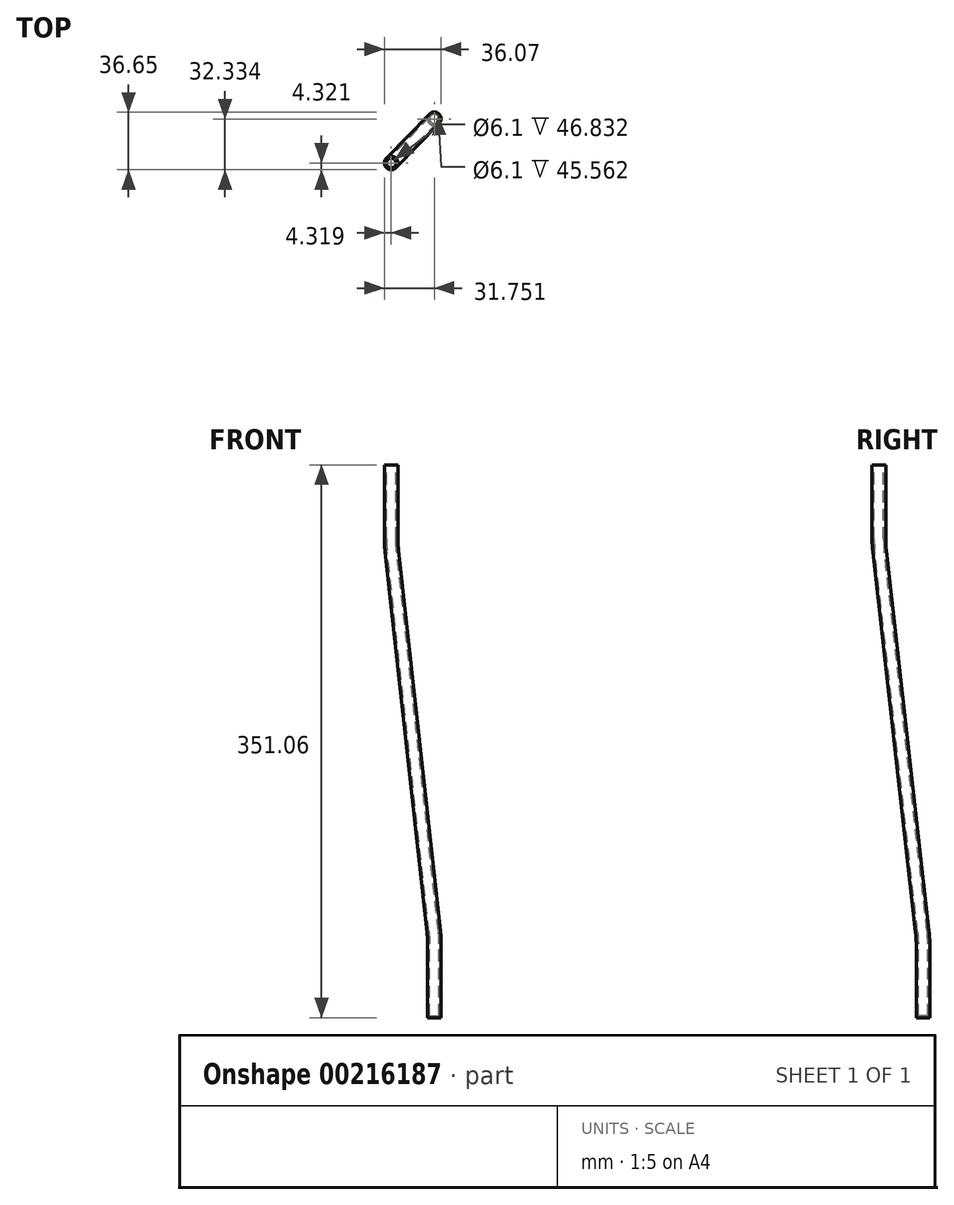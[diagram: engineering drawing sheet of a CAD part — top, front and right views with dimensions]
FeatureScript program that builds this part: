
annotation { "Feature Type Name" : "Feature", "Feature Type Description" : "" }
export const myFeature = defineFeature(function(context is Context, id is Id, definition is map)
    precondition{}
    {
        {
            var Q0;
            Q0=qCreatedBy(makeId("Top.planeOp"),FACE);
            var sketch = newSketch(context, id + "F0", { "sketchPlane" : qUnion([Q0])});
            skLineSegment(sketch, "E0", {"start": v(0, 0) * mm, "end": v(-395.7, 0) * mm});
            skLineSegment(sketch, "E1", {"start": v(-395.7, 0) * mm, "end": v(-395.7, 47.35) * mm});
            skLineSegment(sketch, "E2", {"start": v(0, 0) * mm, "end": v(-368.26, 0) * mm});
            skLineSegment(sketch, "E3", {"start": v(-368.26, 0) * mm, "end": v(-368.26, 75.36) * mm});
            skSolve(sketch);
        }
        {
            var Q0;
            Q0=sQuery(id+"F0.wireOp",EDGE,"E1");
            cPlane(context, id + "F1", {"entities" : qUnion([Q0]), "cplaneType" : CPlaneType.LINE_ANGLE, "offset" : 25.4 * mm, "angle" : 90 * degree, "width" : 152.4 * mm, "height" : 152.4 * mm});
        }
        {
            var Q0;
            Q0=qCreatedBy(id+"F1.planeOp",FACE);
            var sketch = newSketch(context, id + "F2", { "sketchPlane" : qUnion([Q0])});
            skLineSegment(sketch, "E4", {"start": v(47.35, 0) * mm, "end": v(47.35, 982.1) * mm});
            skLineSegment(sketch, "E5", {"start": v(47.35, 982.1) * mm, "end": v(21.95, 982.1) * mm});
            skSolve(sketch);
        }
        {
            var Q0;
            Q0=sQuery(id+"F0.wireOp",EDGE,"E3");
            cPlane(context, id + "F3", {"entities" : qUnion([Q0]), "cplaneType" : CPlaneType.LINE_ANGLE, "offset" : 25.4 * mm, "angle" : 90 * degree, "width" : 152.4 * mm, "height" : 152.4 * mm});
        }
        {
            var Q0;
            Q0=qCreatedBy(id+"F3.planeOp",FACE);
            var sketch = newSketch(context, id + "F4", { "sketchPlane" : qUnion([Q0])});
            skLineSegment(sketch, "E6", {"start": v(75.36, 0) * mm, "end": v(75.36, 631.04) * mm});
            skLineSegment(sketch, "E7", {"start": v(75.36, 631.04) * mm, "end": v(49.96, 631.04) * mm});
            skSolve(sketch);
        }
        {
            var Q0;
            Q0=sQuery(id+"F2.wireOp",EDGE,"E5");
            cPlane(context, id + "F5", {"entities" : qUnion([Q0]), "cplaneType" : CPlaneType.LINE_ANGLE, "offset" : 25.4 * mm, "angle" : 0 * degree, "width" : 152.4 * mm, "height" : 152.4 * mm});
        }
        {
            var Q0;
            Q0=qCreatedBy(id+"F5.planeOp",FACE);
            var sketch = newSketch(context, id + "F6", { "sketchPlane" : qUnion([Q0])});
            skCircle(sketch, "E8", {"center": v(-395.7, -47.35) * mm, "radius": 4.32 * mm});
            skSolve(sketch);
        }
        {
            var Q0;
            Q0=sQuery(id+"F4.wireOp",EDGE,"E7");
            cPlane(context, id + "F7", {"entities" : qUnion([Q0]), "cplaneType" : CPlaneType.LINE_ANGLE, "offset" : 25.4 * mm, "angle" : 0 * degree, "width" : 152.4 * mm, "height" : 152.4 * mm});
        }
        {
            var Q0;
            Q0=qCreatedBy(id+"F7.planeOp",FACE);
            var sketch = newSketch(context, id + "F8", { "sketchPlane" : qUnion([Q0])});
            skCircle(sketch, "E9", {"center": v(-368.26, -75.36) * mm, "radius": 4.32 * mm});
            skSolve(sketch);
        }
        {
            var Q0;
            Q0=sQuery(id+"F2.wireOp",EDGE,"E5");
            var Q1;
            Q1=sQuery(id+"F2.wireOp",EDGE,"E4");
            cPlane(context, id + "F9", {"entities" : qUnion([Q0, Q1]), "cplaneType" : CPlaneType.LINE_ANGLE, "offset" : 25.4 * mm, "angle" : 0 * degree, "width" : 152.4 * mm, "height" : 152.4 * mm});
        }
        {
            var Q0;
            Q0=qCreatedBy(id+"F9.planeOp",FACE);
            var sketch = newSketch(context, id + "F10", { "sketchPlane" : qUnion([Q0])});
            skLineSegment(sketch, "E10", {"start": v(-47.35, 982.1) * mm, "end": v(-47.35, 931.3) * mm});
            skSolve(sketch);
        }
        {
            var Q0;
            Q0=sQuery(id+"F4.wireOp",EDGE,"E6");
            var Q1;
            Q1=sQuery(id+"F4.wireOp",EDGE,"E7");
            cPlane(context, id + "F11", {"entities" : qUnion([Q0, Q1]), "cplaneType" : CPlaneType.LINE_ANGLE, "offset" : 25.4 * mm, "angle" : 0 * degree, "width" : 152.4 * mm, "height" : 152.4 * mm});
        }
        {
            var Q0;
            Q0=qCreatedBy(id+"F11.planeOp",FACE);
            var sketch = newSketch(context, id + "F12", { "sketchPlane" : qUnion([Q0])});
            skLineSegment(sketch, "E11", {"start": v(75.36, 631.04) * mm, "end": v(75.36, 681.84) * mm});
            skSolve(sketch);
        }
        {
            var Q0;
            Q0=sQuery(id+"F10.wireOp",VERTEX,"E10.end");
            var Q1;
            Q1=sQuery(id+"F12.wireOp",VERTEX,"E11.end");
            var Q2;
            Q2=sQuery(id+"F10.wireOp",VERTEX,"E10.start");
            cPlane(context, id + "F13", {"entities" : qUnion([Q0, Q1, Q2]), "cplaneType" : CPlaneType.THREE_POINT, "offset" : 25.4 * mm, "width" : 152.4 * mm, "height" : 152.4 * mm});
        }
        {
            var Q0;
            Q0=qCreatedBy(id+"F13.planeOp",FACE);
            var sketch = newSketch(context, id + "F14", { "sketchPlane" : qUnion([Q0])});
            skLineSegment(sketch, "E12", {"start": v(203.8, 681.84) * mm, "end": v(242.4, 927.38) * mm});
            skLineSegment(sketch, "E13", {"start": v(243.01, 935.27) * mm, "end": v(243.01, 982.1) * mm});
            skPoint(sketch, "E14.visualSharp", {"position": v(243.01, 931.3) * mm});
            skArc(sketch, "E14.filletArc", {"start": v(242.4, 927.38) * mm, "mid": v(242.86, 931.32) * mm, "end": v(243.01, 935.27) * mm});
            skSolve(sketch);
        }
        {
            var Q0;
            Q0=sQuery(id+"F12.wireOp",VERTEX,"E11.start");
            var Q1;
            Q1=sQuery(id+"F14.wireOp",VERTEX,"E12.start");
            var Q2;
            Q2=sQuery(id+"F14.wireOp",VERTEX,"E12.end");
            cPlane(context, id + "F15", {"entities" : qUnion([Q0, Q1, Q2]), "cplaneType" : CPlaneType.THREE_POINT, "offset" : 25.4 * mm, "width" : 152.4 * mm, "height" : 152.4 * mm});
        }
        {
            var Q0;
            Q0=qCreatedBy(id+"F15.planeOp",FACE);
            var sketch = newSketch(context, id + "F16", { "sketchPlane" : qUnion([Q0])});
            skLineSegment(sketch, "E15", {"start": v(203.8, 631.04) * mm, "end": v(203.8, 677.87) * mm});
            skLineSegment(sketch, "E16", {"start": v(204.42, 685.76) * mm, "end": v(242.4, 927.38) * mm});
            skPoint(sketch, "E17.visualSharp", {"position": v(203.8, 681.84) * mm});
            skArc(sketch, "E17.filletArc", {"start": v(204.42, 685.76) * mm, "mid": v(203.96, 681.83) * mm, "end": v(203.8, 677.87) * mm});
            skSolve(sketch);
        }
        {
            var Q0;
            Q0=makeQuery(id+"F8.imprint","IMPRINT",FACE,{"disambiguationData":[TD([[makeQuery(id+"F8.imprint","IMPRINT",EDGE,{"derivedFrom":sQuery(id+"F8.wireOp",EDGE,"E9")}),1.0]])]});
            var Q1;
            Q1=sQuery(id+"F16.wireOp",EDGE,"E15");
            var Q2;
            Q2=sQuery(id+"F16.wireOp",EDGE,"E17.filletArc");
            var Q3;
            Q3=sQuery(id+"F16.wireOp",EDGE,"E16");
            var Q4;
            Q4=sQuery(id+"F14.wireOp",EDGE,"E14.filletArc");
            var Q5;
            Q5=sQuery(id+"F14.wireOp",EDGE,"E13");
            sweep(context, id + "F17", {"profiles" : qUnion([Q0]), "path" : qUnion([Q1, Q2, Q3, Q4, Q5])});
        }
        {
            var Q0;
            Q0=makeQuery(id+"F17.opSweep","CAP_FACE",FACE,{"disambiguationData":[OSD([sQuery(id+"F8.wireOp",EDGE,"E9"),sQuery(id+"F14.wireOp",VERTEX,"E13.end")])],"isStart":false});
            shell(context, id + "F18", {"entities" : qUnion([Q0]), "thickness" : 1.27 * mm});
        }
    });
